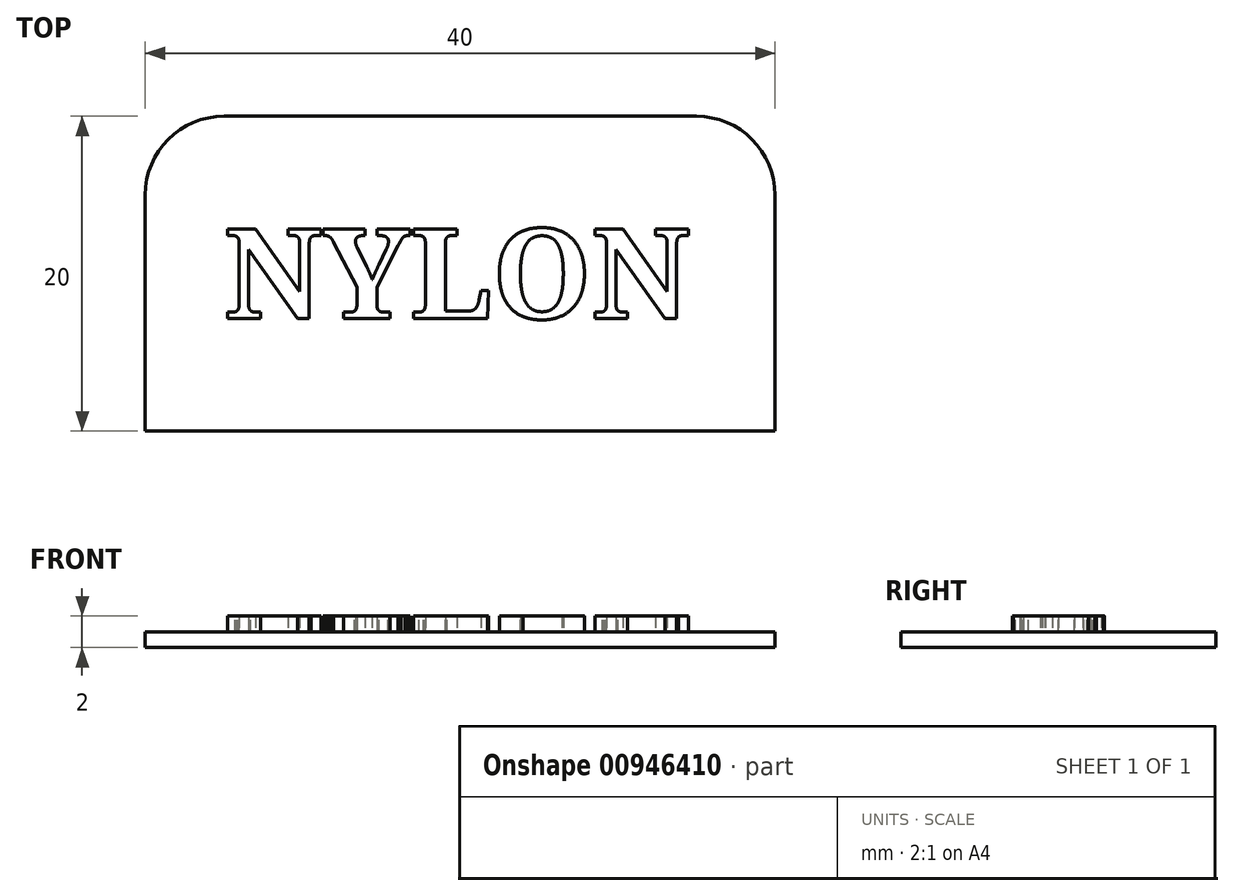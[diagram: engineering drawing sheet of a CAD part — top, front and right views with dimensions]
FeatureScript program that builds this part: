
annotation { "Feature Type Name" : "Feature", "Feature Type Description" : "" }
export const myFeature = defineFeature(function(context is Context, id is Id, definition is map)
    precondition{}
    {
        {
            var Q0;
            Q0=qCreatedBy(makeId("Top.planeOp"),FACE);
            var sketch = newSketch(context, id + "F0", { "sketchPlane" : qUnion([Q0])});
            skLineSegment(sketch, "E0.bottom", {"start": v(-20, 10) * mm, "end": v(20, 10) * mm});
            skLineSegment(sketch, "E0.top", {"start": v(-20, -10) * mm, "end": v(20, -10) * mm});
            skLineSegment(sketch, "E0.left", {"start": v(-20, 10) * mm, "end": v(-20, -10) * mm});
            skLineSegment(sketch, "E0.right", {"start": v(20, 10) * mm, "end": v(20, -10) * mm});
            skPoint(sketch, "E0.middle", {"position": v(0, 0) * mm});
            skSolve(sketch);
        }
        {
            var Q0;
            Q0=makeQuery(id+"F0.imprint","IMPRINT",FACE,{"disambiguationData":[TD([[makeQuery(id+"F0.imprint","IMPRINT",EDGE,{"derivedFrom":sQuery(id+"F0.wireOp",EDGE,"E0.bottom")}),-1.0]])]});
            extrude(context, id + "F1", {"entities" : qUnion([Q0]), "depth" : 1 * mm, "offsetDistance" : 25 * mm});
        }
        {
            var Q0;
            Q0=makeQuery(id+"F1.opExtrude","CAP_FACE",FACE,{"disambiguationData":[OSD([sQuery(id+"F0.wireOp",EDGE,"E0.bottom"),sQuery(id+"F0.wireOp",EDGE,"E0.top"),sQuery(id+"F0.wireOp",EDGE,"E0.left"),sQuery(id+"F0.wireOp",EDGE,"E0.right")])],"isStart":false});
            var sketch = newSketch(context, id + "F2", { "sketchPlane" : qUnion([Q0])});
            skText(sketch, "E1", { "text": "NYLON", "fontName": "NotoSerif-Bold.ttf"});
            const initialGuessF2  = {"E1": [-0.015, -0.00286, 1, 0, 0.00575]};
            skSetInitialGuess(sketch, initialGuessF2);
            skSolve(sketch);
        }
        {
            var Q0;
            Q0=qSketchRegion(id+"F2",true);
            extrude(context, id + "F3", {"entities" : qUnion([Q0]), "operationType" : NewBodyOperationType.ADD, "depth" : 1 * mm, "offsetDistance" : 25 * mm});
        }
        {
            var Q0;
            Q0=makeQuery(id+"F1.opExtrude","SWEPT_EDGE",EDGE,{"disambiguationData":[OSD([sQuery(id+"F0.wireOp",EDGE,"E0.bottom"),sQuery(id+"F0.wireOp",EDGE,"E0.left")])]});
            var Q1;
            Q1=makeQuery(id+"F1.opExtrude","SWEPT_EDGE",EDGE,{"disambiguationData":[OSD([sQuery(id+"F0.wireOp",EDGE,"E0.bottom"),sQuery(id+"F0.wireOp",EDGE,"E0.right")])]});
            fillet(context, id + "F4", {"entities" : qUnion([Q0, Q1]), "radius" : 5 * mm, "tangentPropagation" : true, "allowEdgeOverflow" : false});
        }
    });
